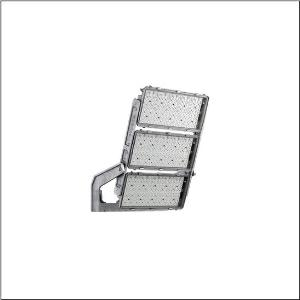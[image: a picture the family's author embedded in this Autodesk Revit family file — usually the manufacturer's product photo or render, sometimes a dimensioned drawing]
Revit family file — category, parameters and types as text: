
# Revit family: floodlight_fl_11_maxi_pro_remote___pl64_5xa779524e01ba_e2b2
name_source: partatom
category: Lighting Fixtures
units: mm (PartAtom-declared; Revit-internal decimal feet)

## family parameters
Cut with Voids When Loaded = No
Host = Face
Light Source = No
Part Type = Normal
Room Calculation Point = No
Round Connector Dimension = Use Diameter
Shared = No

## types (1)
- --- (1 x LED, 107650 lm, 1020.5 W, 5700K)
    Apparent Load = 1020 VA
    CIE Flux Codes = 28 80 98 100 100
    Color Rendering = 90
    Color Temperature = 5700K
    Default Elevation = 1800 mm
    Description = Floodlight FL 11  maxi  pro Remote floodlight; light control with lens of PMMA; cover panel of toughened safety glass, transparent; light distribution: PL64, asymmetric direct distribution, LEDcolour temperature: 5700K, rated luminous flux: 107.650lm, colour rendering: CRI > 90, light colour: 957; luminous efficacy: 106lm/W; brightness control: DMX+RDM; with terminal, 8-pole, max. 2.5mm², mains connection: 220..240V/380..400V AC, 50/60Hz, surge voltage resistance: line to ground: 10kV, ECG replaceable separately, LED unit replaceable without ESD environment, dustproof LED module, dimming range 10..100%; 1021W floodlight with 3x LED unit of diecast aluminium, coated grey; length: 713mm / width: 651mm / height: 338mm; mounting bracket, of diecast aluminium, uncoated, natural, equipment: Longlife, protection rating (complete): IP66; insulation class (complete): insulation class I (protective earthing); certification: CE, ENEC, VDE; ball protection: ball impact resistance with accessories, impact resistance: IK07; only for outdoor installations, rated ambient temperature 10°C, permissible operating ambient temperature: -40..+40°C, permissible storage temperature: -40..+85°C; packaging unit: 1 piece

Light Distribution: PL64
    Height = 320 mm
    Lamp = 1 x LED
    Lamp Light Flux = 107650 lm
    Lamp Power = 1020.5 W
    Lamp count = 1
    Length = 1002 mm
    Luminous efficacy = 105 lm/W
    Manufacturer = Siteco
    ModVariant = No
    Model = 5XA779524E01BA
    Mounting Place = Ceiling
    Mounting Type = Surface mounted
    Number of Poles = 1
    OnlyDefault = Yes
    Power Factor = 1
    Product Name = Floodlight FL 11 maxi pro Remote | PL64
    Product group = floodlight | ceiling mounted
    ProductGroupID = 303
    Protection Class = Protection class I
    Protection Degree = IP 66
    RLX_Detail_Level = 1
    RLX_Emergency_Light_Flux = 0 lm
    RLX_Emergency_Type = 0
    RLX_Emergency_Type_DB = No
    RlxData = <blob elided: 52329 chars, md5=ec202022>
    Socket = socket
    Standby Power = 0 W
    System Light Flux = 107650 lm
    System Power = 1020 W
    Type Comments = factory setting: luminous flux: 100 % | dim-lin: 255 | 710 mA
    Type Image = l_1006784.jpg
    URL = http://relux.com
    VarID = @adj_045719
    Voltage = 0 V
    Weight = 0.00 kg
    Width = 655 mm

## geometry (parser evidence)
native form markers: Blend x4, Sweep x14
no freeform markers — native parametric forms only
